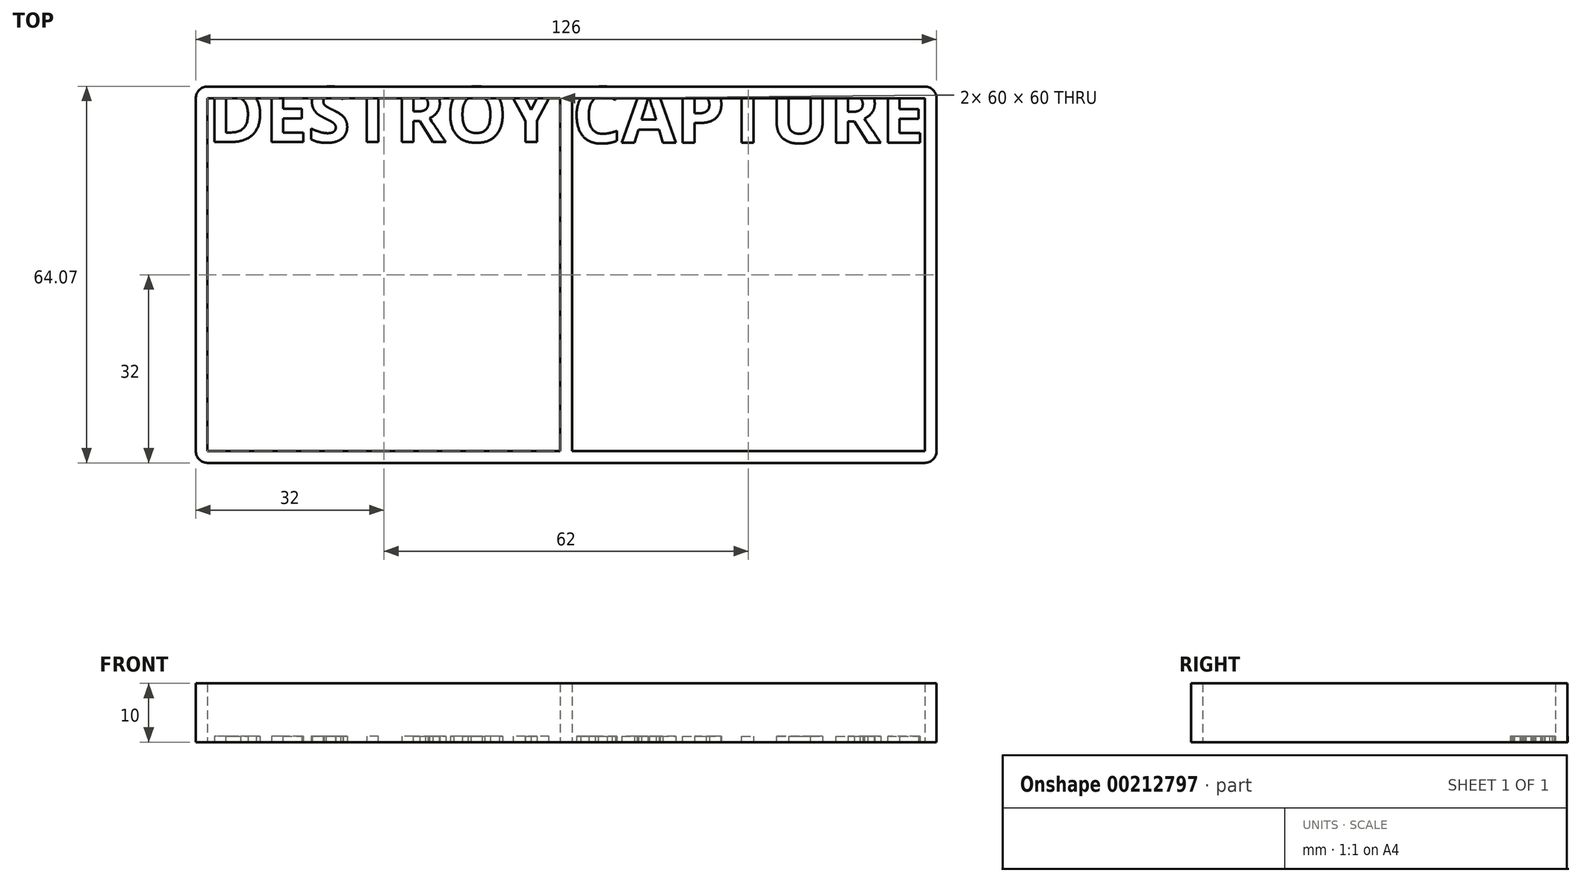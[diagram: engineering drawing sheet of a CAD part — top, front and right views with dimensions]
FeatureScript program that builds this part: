
annotation { "Feature Type Name" : "Feature", "Feature Type Description" : "" }
export const myFeature = defineFeature(function(context is Context, id is Id, definition is map)
    precondition{}
    {
        {
            assignVariable(context, id + "F0", {"name" : "THICKNESS", "anyValue" : 2});
        }
        {
            var Q0;
            Q0=qCreatedBy(makeId("Top.planeOp"),FACE);
            var sketch = newSketch(context, id + "F1", { "sketchPlane" : qUnion([Q0])});
            skLineSegment(sketch, "E0.bottom", {"start": v(-1, 30) * mm, "end": v(-61, 30) * mm});
            skLineSegment(sketch, "E0.top", {"start": v(-1, -30) * mm, "end": v(-61, -30) * mm});
            skLineSegment(sketch, "E0.left", {"start": v(-1, 30) * mm, "end": v(-1, -30) * mm});
            skLineSegment(sketch, "E0.right", {"start": v(-61, 30) * mm, "end": v(-61, -30) * mm});
            skPoint(sketch, "E0.middle", {"position": v(-31, 0) * mm});
            skLineSegment(sketch, "E1.bottom", {"start": v(1, 30) * mm, "end": v(61, 30) * mm});
            skLineSegment(sketch, "E1.top", {"start": v(1, -30) * mm, "end": v(61, -30) * mm});
            skLineSegment(sketch, "E1.left", {"start": v(1, 30) * mm, "end": v(1, -30) * mm});
            skLineSegment(sketch, "E1.right", {"start": v(61, 30) * mm, "end": v(61, -30) * mm});
            skPoint(sketch, "E1.middle", {"position": v(31, 0) * mm});
            skLineSegment(sketch, "E2.bottom", {"start": v(-63, 32) * mm, "end": v(63, 32) * mm});
            skLineSegment(sketch, "E2.top", {"start": v(-63, -32) * mm, "end": v(63, -32) * mm});
            skLineSegment(sketch, "E2.left", {"start": v(-63, 32) * mm, "end": v(-63, -32) * mm});
            skLineSegment(sketch, "E2.right", {"start": v(63, 32) * mm, "end": v(63, -32) * mm});
            skPoint(sketch, "E2.middle", {"position": v(0, 0) * mm});
            skSolve(sketch);
        }
        {
            var Q0;
            Q0 = qSketchRegion(id + "F1", true);
            extrude(context, id + "F2", {"entities" : qUnion([Q0]), "depth" : 10 * mm});
        }
        {
            var Q0;
            Q0=qCreatedBy(makeId("Top.planeOp"),FACE);
            var sketch = newSketch(context, id + "F3", { "sketchPlane" : qUnion([Q0])});
            skText(sketch, "E3", { "text": "DESTROY", "fontName": "OpenSans-Bold.ttf"});
            skText(sketch, "E4", { "text": "CAPTURE", "fontName": "OpenSans-Bold.ttf"});
            const initialGuessF3  = {"E3": [-0.061, 0.02256, 1, 0, 0.00944], "E4": [0.001, 0.02243, 1, 0, 0.00957]};
            skSetInitialGuess(sketch, initialGuessF3);
            skSolve(sketch);
        }
        {
            var Q0;
            Q0 = qSketchRegion(id + "F3", true);
            extrude(context, id + "F4", {"entities" : qUnion([Q0]), "operationType" : NewBodyOperationType.ADD, "depth" : 1 * mm});
        }
        {
            var Q0;
            Q0=makeQuery(id+"F2.opExtrude","SWEPT_EDGE",EDGE,{"disambiguationData":[OSD([sQuery(id+"F1.wireOp",EDGE,"E2.bottom"),sQuery(id+"F1.wireOp",EDGE,"E2.left")])]});
            var Q1;
            Q1=makeQuery(id+"F2.opExtrude","SWEPT_EDGE",EDGE,{"disambiguationData":[OSD([sQuery(id+"F1.wireOp",EDGE,"E2.top"),sQuery(id+"F1.wireOp",EDGE,"E2.left")])]});
            var Q2;
            Q2=makeQuery(id+"F2.opExtrude","SWEPT_EDGE",EDGE,{"disambiguationData":[OSD([sQuery(id+"F1.wireOp",EDGE,"E2.top"),sQuery(id+"F1.wireOp",EDGE,"E2.right")])]});
            var Q3;
            Q3=makeQuery(id+"F2.opExtrude","SWEPT_EDGE",EDGE,{"disambiguationData":[OSD([sQuery(id+"F1.wireOp",EDGE,"E2.bottom"),sQuery(id+"F1.wireOp",EDGE,"E2.right")])]});
            fillet(context, id + "F5", {"entities" : qUnion([Q0, Q1, Q2, Q3]), "radius" : (getVariable(context, 'THICKNESS')) * mm, "tangentPropagation" : true, "allowEdgeOverflow" : false});
        }
    });
